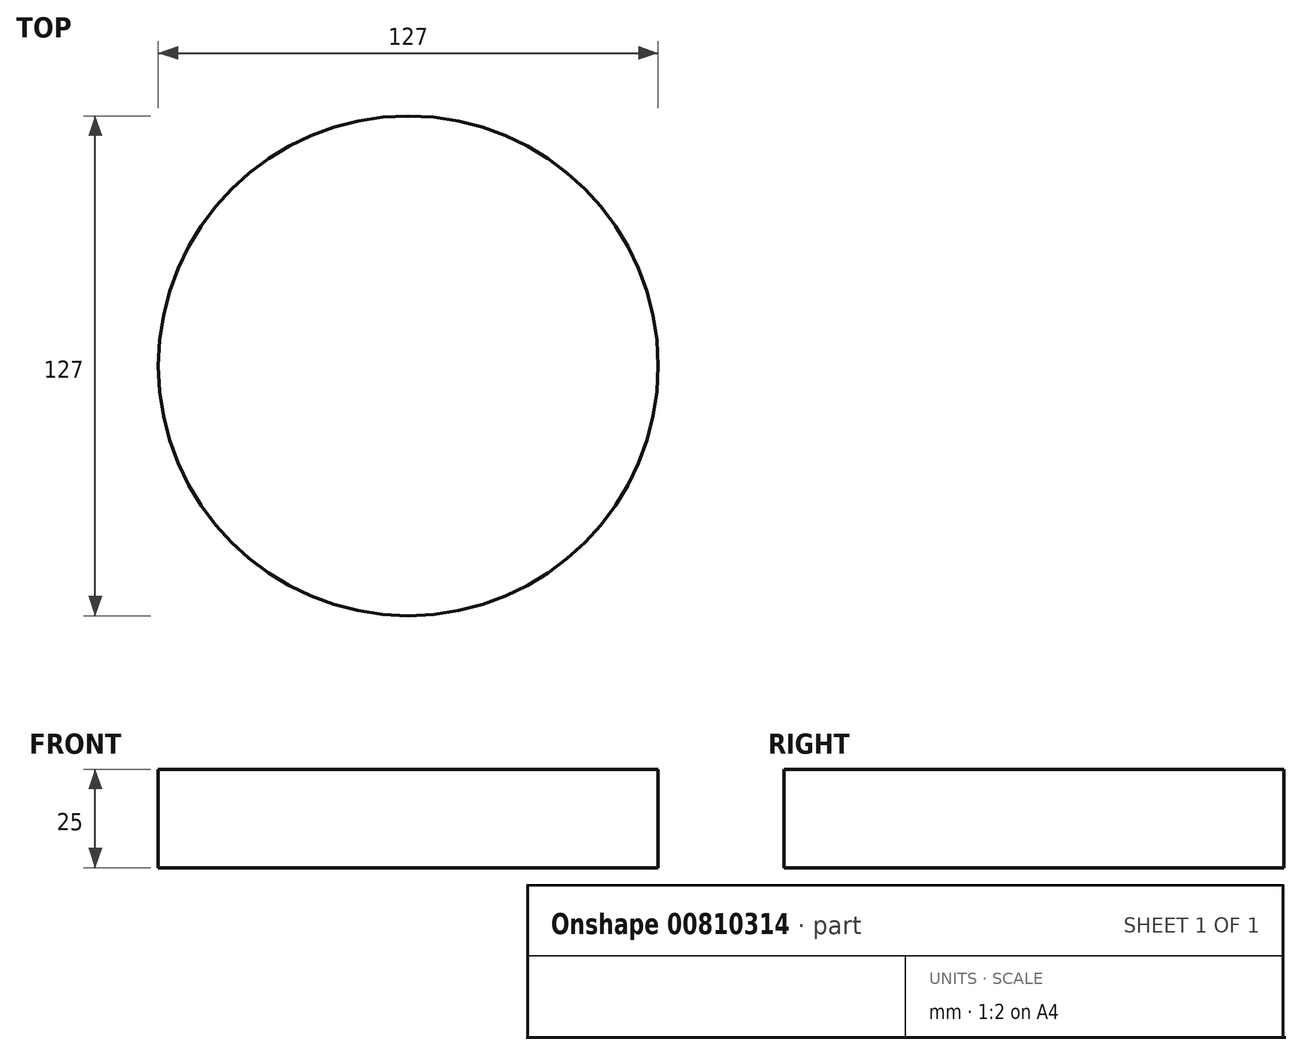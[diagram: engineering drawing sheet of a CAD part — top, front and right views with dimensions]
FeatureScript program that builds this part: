
annotation { "Feature Type Name" : "Feature", "Feature Type Description" : "" }
export const myFeature = defineFeature(function(context is Context, id is Id, definition is map)
    precondition{}
    {
        {
            var Q0;
            Q0=qCreatedBy(makeId("Top.planeOp"),FACE);
            var sketch = newSketch(context, id + "F0", { "sketchPlane" : qUnion([Q0])});
            skCircle(sketch, "E0", {"center": v(0, 0) * mm, "radius": 63.5 * mm});
            skSolve(sketch);
        }
        {
            var Q0;
            Q0=makeQuery(id+"F0.imprint","IMPRINT",FACE,{"disambiguationData":[TD([[makeQuery(id+"F0.imprint","IMPRINT",EDGE,{"derivedFrom":sQuery(id+"F0.wireOp",EDGE,"E0")}),1.0]])]});
            extrude(context, id + "F1", {"entities" : qUnion([Q0]), "depth" : 25 * mm, "offsetDistance" : 25 * mm});
        }
    });
